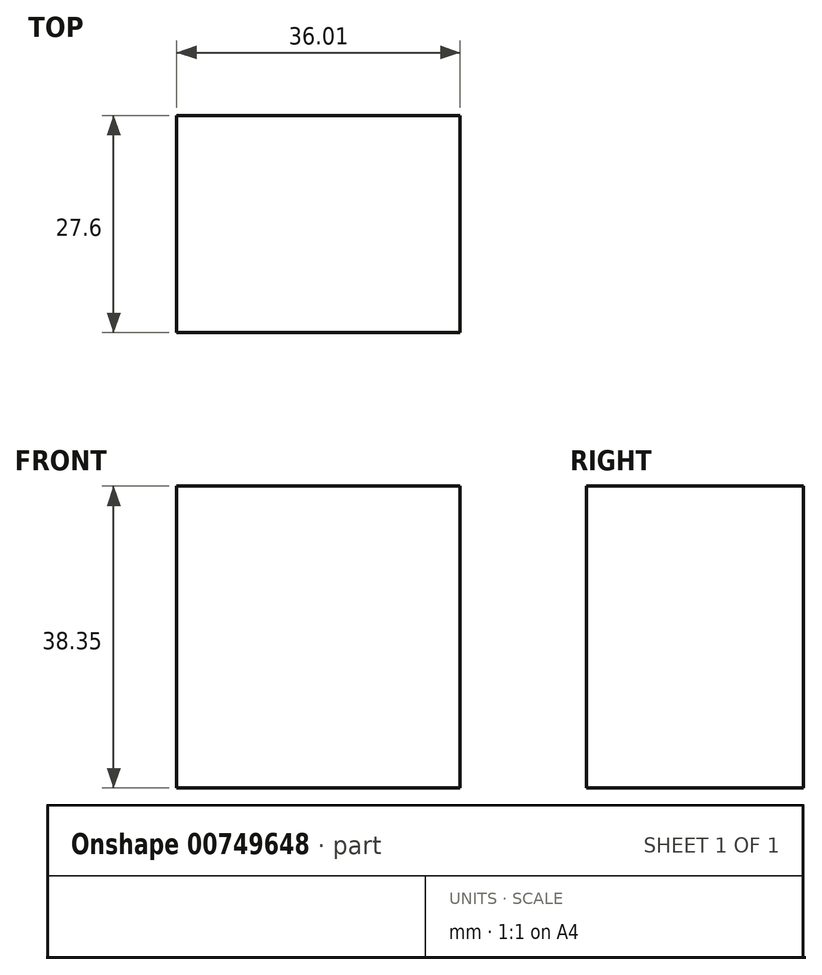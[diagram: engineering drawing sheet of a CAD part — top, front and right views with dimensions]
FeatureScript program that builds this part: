
annotation { "Feature Type Name" : "Feature", "Feature Type Description" : "" }
export const myFeature = defineFeature(function(context is Context, id is Id, definition is map)
    precondition{}
    {
        {
            var Q0;
            Q0=qCreatedBy(makeId("Top.planeOp"),FACE);
            var sketch = newSketch(context, id + "F0", { "sketchPlane" : qUnion([Q0])});
            skLineSegment(sketch, "E0.bottom", {"start": v(-47.7, 33.99) * mm, "end": v(-11.7, 33.99) * mm});
            skLineSegment(sketch, "E0.top", {"start": v(-47.7, 6.4) * mm, "end": v(-11.7, 6.4) * mm});
            skLineSegment(sketch, "E0.left", {"start": v(-47.7, 33.99) * mm, "end": v(-47.7, 6.4) * mm});
            skLineSegment(sketch, "E0.right", {"start": v(-11.7, 33.99) * mm, "end": v(-11.7, 6.4) * mm});
            skSolve(sketch);
        }
        {
            var Q0;
            Q0 = qSketchRegion(id + "F0", true);
            extrude(context, id + "F1", {"entities" : qUnion([Q0]), "depth" : 38.35 * mm, "offsetDistance" : 25.4 * mm});
        }
    });
